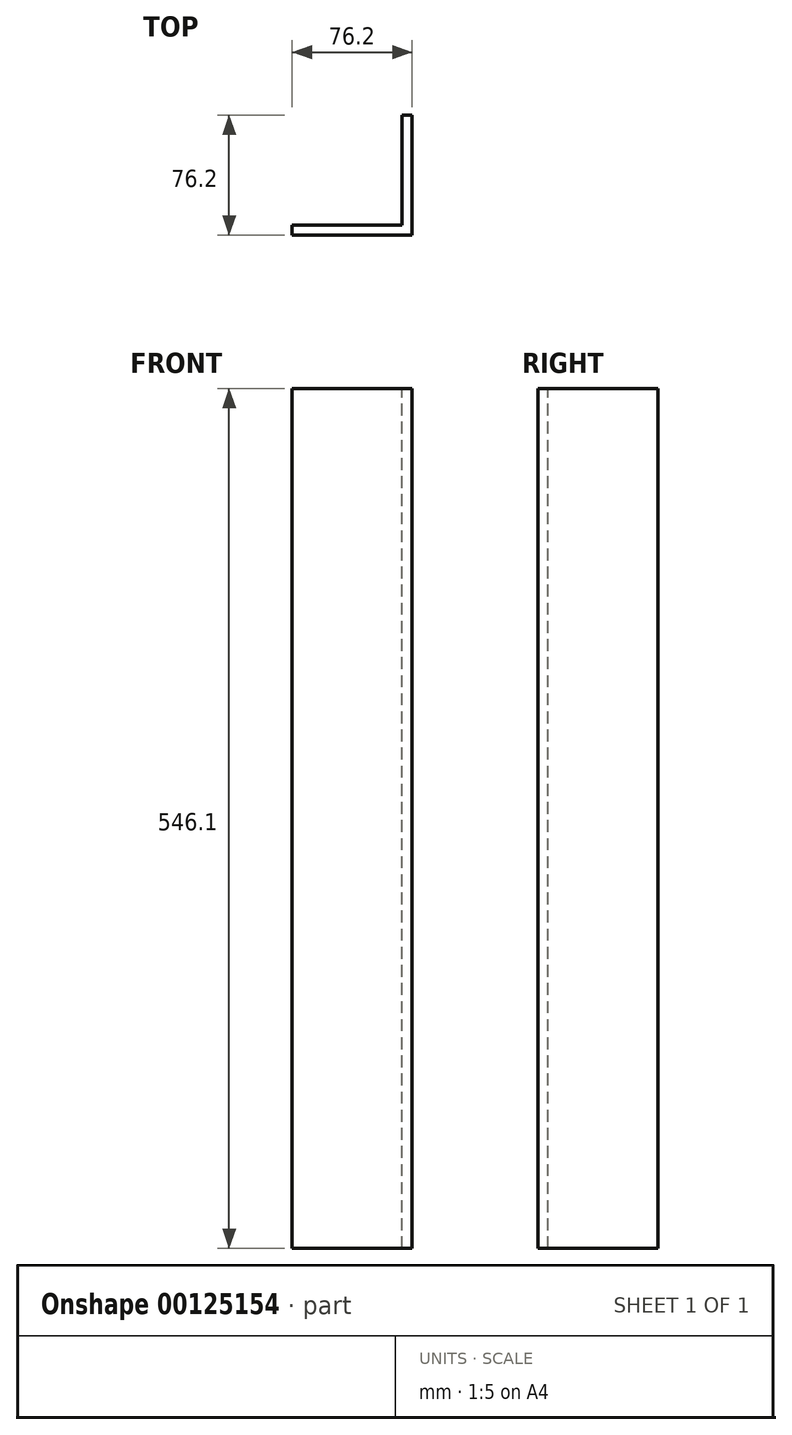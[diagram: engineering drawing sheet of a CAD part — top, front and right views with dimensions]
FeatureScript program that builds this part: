
annotation { "Feature Type Name" : "Feature", "Feature Type Description" : "" }
export const myFeature = defineFeature(function(context is Context, id is Id, definition is map)
    precondition{}
    {
        {
            var Q0;
            Q0=qCreatedBy(makeId("Top.planeOp"),FACE);
            var sketch = newSketch(context, id + "F0", { "sketchPlane" : qUnion([Q0])});
            skLineSegment(sketch, "E0", {"start": v(-76.2, 0) * mm, "end": v(0, 0) * mm});
            skLineSegment(sketch, "E1", {"start": v(0, 0) * mm, "end": v(0, 76.2) * mm});
            skLineSegment(sketch, "E2.0", {"start": v(-6.35, 6.35) * mm, "end": v(-6.35, 76.2) * mm});
            skLineSegment(sketch, "E2.1", {"start": v(-76.2, 6.35) * mm, "end": v(-6.35, 6.35) * mm});
            skLineSegment(sketch, "E3", {"start": v(-6.35, 76.2) * mm, "end": v(0, 76.2) * mm});
            skLineSegment(sketch, "E4", {"start": v(-76.2, 6.35) * mm, "end": v(-76.2, 0) * mm});
            skSolve(sketch);
        }
        {
            var Q0;
            Q0=qSketchRegion(id+"F0",true);
            extrude(context, id + "F1", {"entities" : qUnion([Q0]), "oppositeDirection" : true, "depth" : 546.1 * mm});
        }
    });
